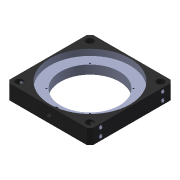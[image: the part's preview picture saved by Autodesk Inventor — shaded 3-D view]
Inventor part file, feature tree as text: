
AUTODESK INVENTOR PART (.ipt)
format: ipt  version: 2019 (Build 230136000, 136)  size: 401,920 bytes
history: native  units: mm
features: other x10, imported_body x9, sketch x3, extrude x2, projected_geometry x2, hole x1
ambient origin geometry x8: Origin, YZ Plane, XZ Plane, XY Plane, X Axis, Y Axis, Z Axis, Center Point
bodies: Body1 (feature_tree), Body2 (feature_tree), Body3 (feature_tree), Body4 (feature_tree), Body5 (feature_tree), Body6 (feature_tree), Body7 (feature_tree), Body8 (feature_tree), Body9 (feature_tree)
feature tree (27):
  other  "13108-001-1-solid1"
  other  "13108-E0W1"
  extrude  "Extrusion1"  Depth=5.25mm TaperAngle=0.0deg
  extrude  "Extrusion2"  Depth=4.0mm TaperAngle=0.0deg
  hole  "Hole1"  [1 undecoded]
  other  "SS4S019-1-1-solid1"
  other  "SS4S019-1-2-solid1"
  other  "SS4S019-1-3-solid1"
  other  "SS4S019-1-4-solid1"
  other  "SS4S019-1-5-solid1"
  other  "SS4S019-1-6-solid1"
  other  "SS4S019-1-7-solid1"
  other  "SS4S019-1-8-solid1"
  imported_body  "Base1"
  imported_body  "Base2"
  imported_body  "Base3"
  imported_body  "Base4"
  imported_body  "Base5"
  imported_body  "Base6"
  imported_body  "Base7"
  imported_body  "Base8"
  imported_body  "Base9"
  sketch  "Sketch1"  dims[d1=68.0mm d2=5.25mm d3=0.0mm]
  projected_geometry  "Projected Loop1"
  sketch  "Sketch2"  dims[d4=50.0mm d5=4.0mm d6=0.0mm]
  sketch  "Sketch3"  dims[d7=36.99764mm d8=36.99764mm d9=1.3208mm d10=3.4036mm d11=9.525mm d12=6.35mm d13=14.3117mm d14=5.5118mm d15=20.594885mm]
  projected_geometry  "Projected Loop2"
note: 1 required parameter value undecoded (feature->parameter linkage not recoverable at this tier; creation-order binding heuristic only, values carry confidence <= 0.55)
